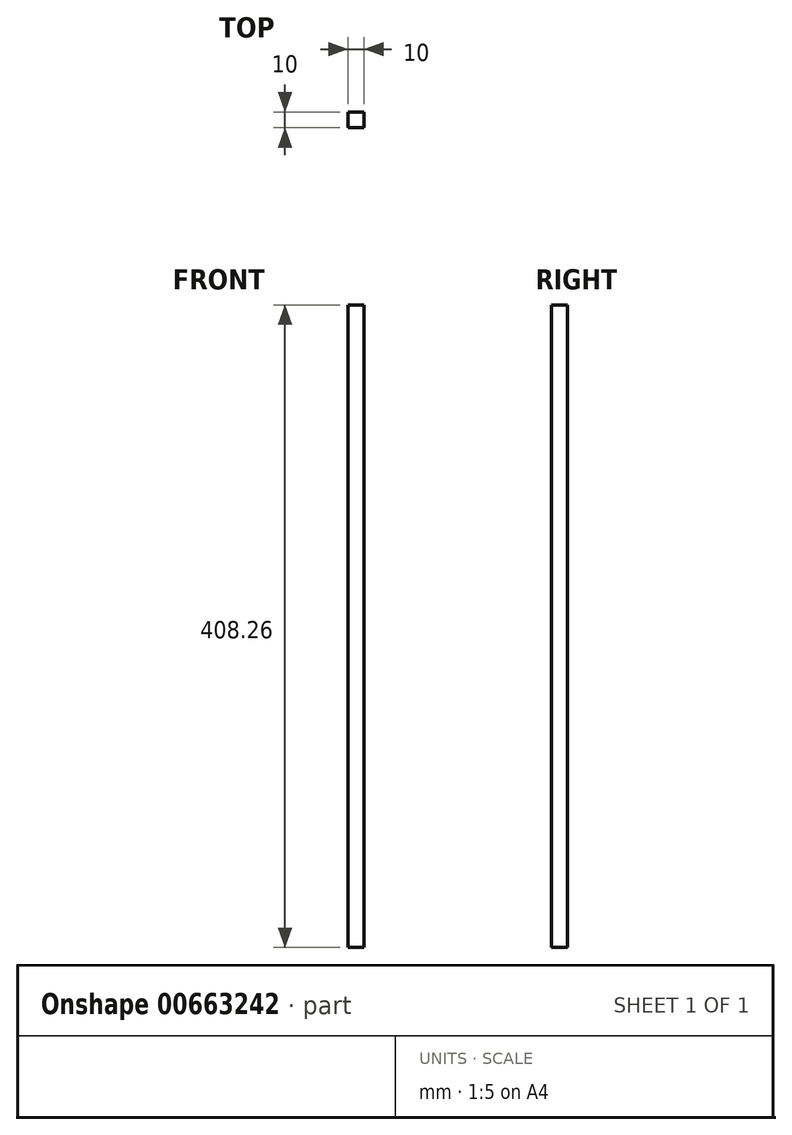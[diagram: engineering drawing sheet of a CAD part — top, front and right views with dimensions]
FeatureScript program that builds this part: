
annotation { "Feature Type Name" : "Feature", "Feature Type Description" : "" }
export const myFeature = defineFeature(function(context is Context, id is Id, definition is map)
    precondition{}
    {
        {
            var Q0;
            Q0=qCreatedBy(makeId("Top.planeOp"),FACE);
            var sketch = newSketch(context, id + "F0", { "sketchPlane" : qUnion([Q0])});
            skLineSegment(sketch, "E0.bottom", {"start": v(5, 5) * mm, "end": v(-5, 5) * mm});
            skLineSegment(sketch, "E0.top", {"start": v(5, -5) * mm, "end": v(-5, -5) * mm});
            skLineSegment(sketch, "E0.left", {"start": v(5, 5) * mm, "end": v(5, -5) * mm});
            skLineSegment(sketch, "E0.right", {"start": v(-5, 5) * mm, "end": v(-5, -5) * mm});
            skPoint(sketch, "E0.middle", {"position": v(0, 0) * mm});
            skSolve(sketch);
        }
        {
            var Q0;
            Q0 = qSketchRegion(id + "F0", true);
            extrude(context, id + "F1", {"entities" : qUnion([Q0]), "depth" : 408.26 * mm, "offsetDistance" : 25 * mm});
        }
    });
